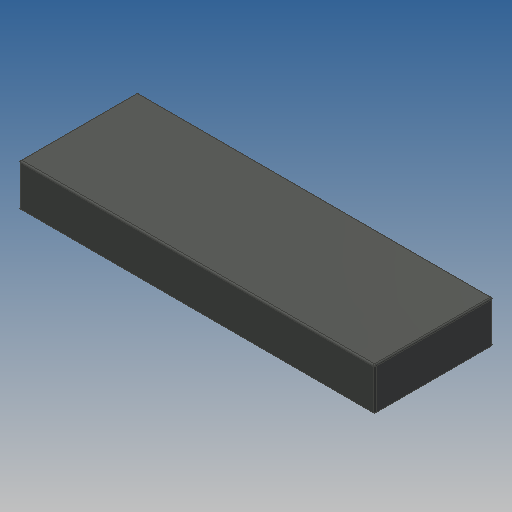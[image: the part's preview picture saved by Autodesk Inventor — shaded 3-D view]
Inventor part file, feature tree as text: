
AUTODESK INVENTOR PART (.ipt)
format: ipt  version: 2022.2 (Build 262287000, 287)  size: 160,768 bytes
history: native  units: in
note: dims shown in document units (in); Inventor stores cm internally (conversion verified against a paired STEP export)
features: extrude x3, sketch x2, other x2, fillet x1
ambient origin geometry x8: Origin, YZ Plane, XZ Plane, XY Plane, X Axis, Y Axis, Z Axis, Center Point
bodies: Solid1 (feature_tree)
feature tree (8):
  extrude  "Extrusion1"  Depth=0.315in
  sketch  "Sketch3"  dims[d4=0.126in d5=0.0in d7=0.0591in d8=0.063in d11=0.063in d12=0.0in d22=0.0039in d60=0.2564in d61=0.189in d62=0.063in d75=0.315in d76=0.315in d86=0.126in d89=0.315in d90=0.0in d91=0.0in d92=0.0in d93=0.0in d94=0.0in d95=0.0157in d96=0.0157in d97=0.0157in d98=0.0in]
  extrude  "Extrusion2"  Depth=0.063in
  extrude  "Extrusion7"  Depth=0.063in TaperAngle=0.0deg
  fillet  "Fillet1"  Radius=0.0039in
  other  "Work Axis1"
  other  "Work Axis2"
  sketch  "Sketch2"  dims[d0=0.9449in d1=0.315in]
